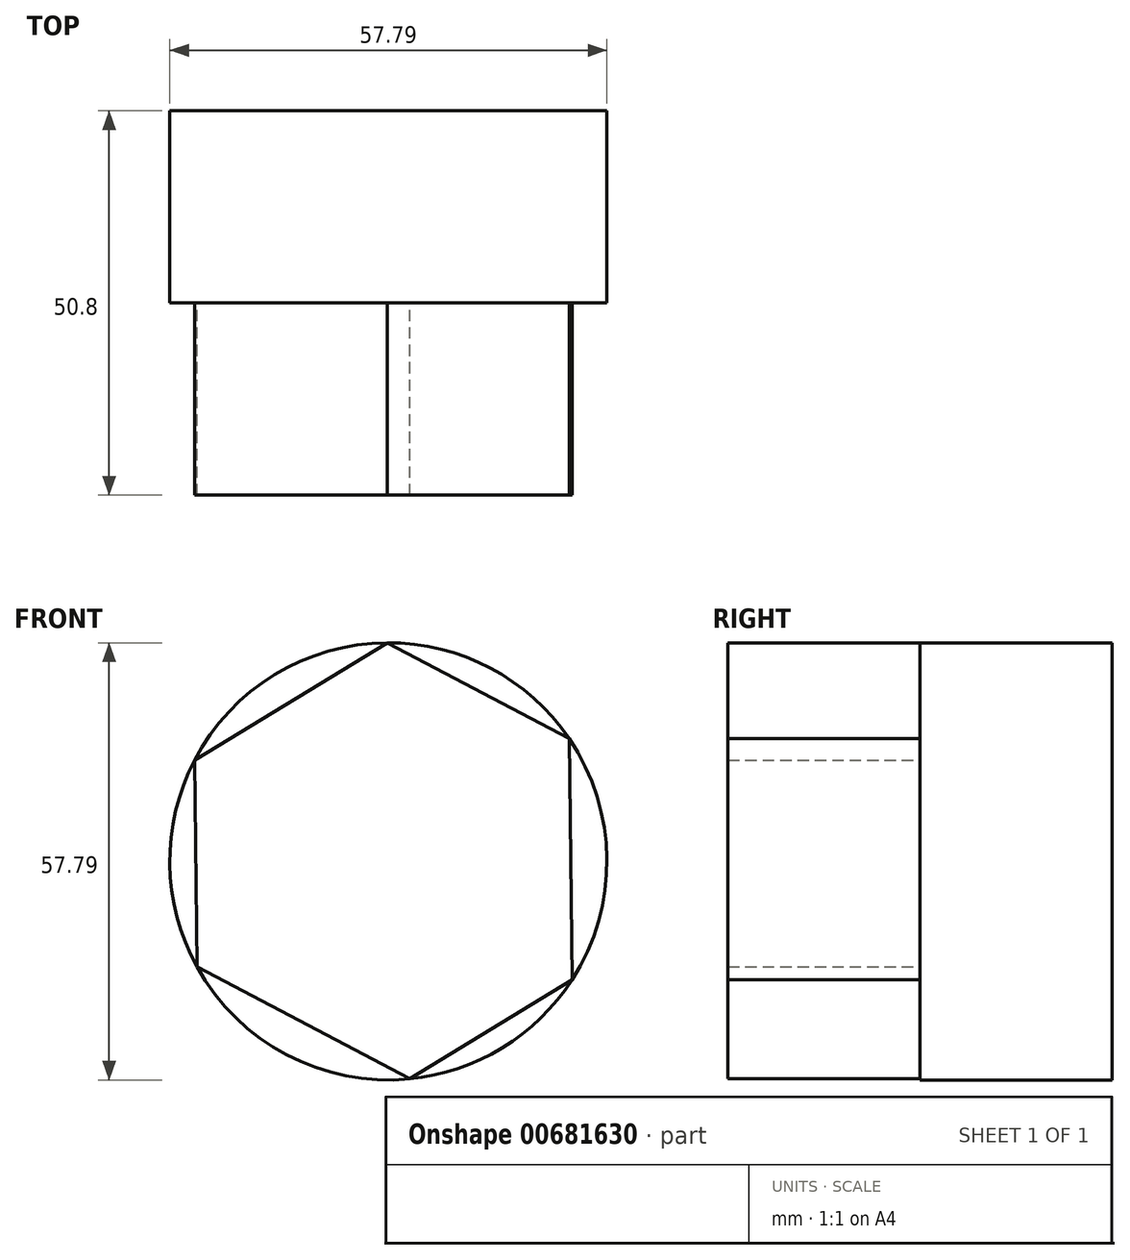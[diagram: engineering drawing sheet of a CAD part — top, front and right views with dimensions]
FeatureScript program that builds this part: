
annotation { "Feature Type Name" : "Feature", "Feature Type Description" : "" }
export const myFeature = defineFeature(function(context is Context, id is Id, definition is map)
    precondition{}
    {
        {
            var Q0;
            Q0=qCreatedBy(makeId("Front.planeOp"),FACE);
            var sketch = newSketch(context, id + "F0", { "sketchPlane" : qUnion([Q0])});
            skCircle(sketch, "E0", {"center": v(-55.2, 41.44) * mm, "radius": 28.9 * mm});
            skSolve(sketch);
        }
        {
            var Q0;
            Q0=makeQuery(id+"F0.imprint","IMPRINT",FACE,{"disambiguationData":[TD([[makeQuery(id+"F0.imprint","IMPRINT",EDGE,{"derivedFrom":sQuery(id+"F0.wireOp",EDGE,"E0")}),1.0]])]});
            extrude(context, id + "F1", {"entities" : qUnion([Q0]), "depth" : 25.4 * mm, "offsetDistance" : 25.4 * mm});
        }
        {
            var Q0;
            Q0=makeQuery(id+"F1.opExtrude","CAP_FACE",FACE,{"disambiguationData":[OSD([sQuery(id+"F0.wireOp",EDGE,"E0")])],"isStart":false});
            var sketch = newSketch(context, id + "F2", { "sketchPlane" : qUnion([Q0])});
            skLineSegment(sketch, "E1", {"start": v(-31.3, 57.67) * mm, "end": v(-30.93, 25.78) * mm});
            skLineSegment(sketch, "E2", {"start": v(-30.93, 25.78) * mm, "end": v(-52.38, 12.69) * mm});
            skLineSegment(sketch, "E3", {"start": v(-52.38, 12.69) * mm, "end": v(-80.5, 27.49) * mm});
            skLineSegment(sketch, "E4", {"start": v(-80.5, 27.49) * mm, "end": v(-80.83, 54.8) * mm});
            skLineSegment(sketch, "E5", {"start": v(-80.83, 54.8) * mm, "end": v(-55.37, 70.34) * mm});
            skLineSegment(sketch, "E6", {"start": v(-55.37, 70.34) * mm, "end": v(-31.3, 57.67) * mm});
            skSolve(sketch);
        }
        {
            var Q0;
            Q0=makeQuery(id+"F2.imprint","IMPRINT",FACE,{"disambiguationData":[TD([[makeQuery(id+"F2.imprint","IMPRINT",EDGE,{"derivedFrom":sQuery(id+"F2.wireOp",EDGE,"E1")}),-1.0]])]});
            extrude(context, id + "F3", {"entities" : qUnion([Q0]), "operationType" : NewBodyOperationType.ADD, "depth" : 25.4 * mm, "offsetDistance" : 25.4 * mm});
        }
    });
